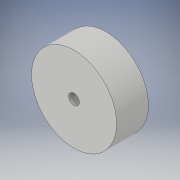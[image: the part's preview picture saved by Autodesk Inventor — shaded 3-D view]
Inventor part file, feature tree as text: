
AUTODESK INVENTOR PART (.ipt)
format: ipt  version: 2017 (Build 210142000, 142)  size: 98,304 bytes
history: native  units: in
note: dims shown in document units (in); Inventor stores cm internally (conversion verified against a paired STEP export)
features: sketch x2, extrude x1, hole x1
ambient origin geometry x8: Origin, YZ Plane, XZ Plane, XY Plane, X Axis, Y Axis, Z Axis, Center Point
bodies: Solid1 (feature_tree)
feature tree (4):
  extrude  "Extrusion1"  Depth=1.5in TaperAngle=0.0deg
  hole  "Hole1"  [1 undecoded]
  sketch  "Sketch3"  dims[d1=4.0in d2=1.5in d3=0.0in]
  sketch  "Sketch4"  dims[d4=0.5in d5=0.5in d6=0.75in d7=0.375in d8=0.25in d9=0.5635in d10=1.0in d11=0.8108in]
note: 1 required parameter value undecoded (feature->parameter linkage not recoverable at this tier; creation-order binding heuristic only, values carry confidence <= 0.55)
